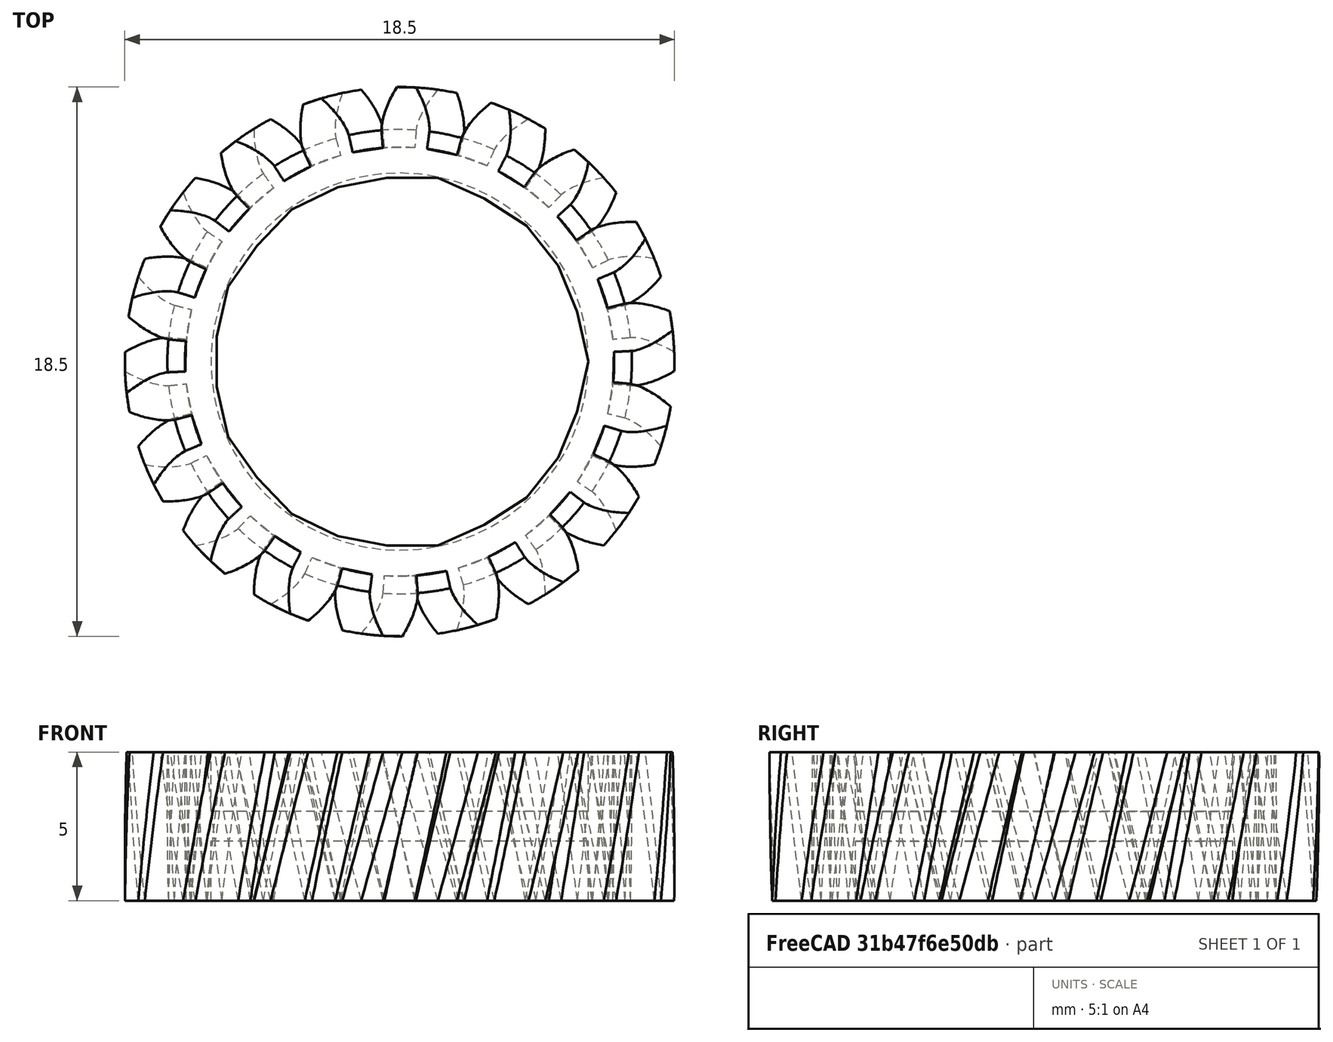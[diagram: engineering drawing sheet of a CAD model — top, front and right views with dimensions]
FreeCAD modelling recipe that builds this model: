
FCSTD DOCUMENT  (FreeCAD 0.15R4671 (Git))
Label: Idlegear B
License: All rights reserved
LicenseURL: http://en.wikipedia.org/wiki/All_rights_reserved
objects: Part::Cylinder×2, Part::Cut×2, Part::FeaturePython×1
note: 5 computed .brp shape members not serialized (recipe doc carries the construction recipe); baked Part::Feature solids carry a one-line shape summary decoded from their .brp

FEATURE [Part::FeaturePython] InvoluteGear  # WARN: FeaturePython — macro-defined, semantics opaque (R4)
  backlash = 0
  beta = 14
  clearance = 0.25
  double_helix = false
  head = 0
  height = 5
  module = 0.9
  numpoints = 6
  pressure_angle = 20
  reversed_backlash = false
  shift = 0
  simple = false
  teeth = 18
  undercut = false
FEATURE [Part::Cylinder] Cylinder  label="CentreDiscH1"
  Angle = 360
  Height = 2
  Radius = 6.35
FEATURE [Part::Cut] Cut
  Base = -> InvoluteGear
  Tool = -> Cylinder
FEATURE [Part::Cylinder] Cylinder001  label="CentreDiscH2"
  Angle = 360
  Height = 2.5
  Placement = pos=(0,0,3) rot=(0,0,1;0rad)
  Radius = 6.35
FEATURE [Part::Cut] Cut001
  Base = -> Cut
  Tool = -> Cylinder001
